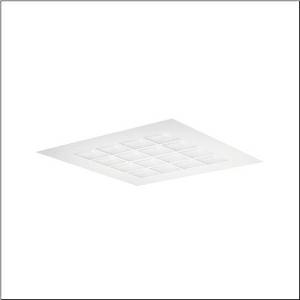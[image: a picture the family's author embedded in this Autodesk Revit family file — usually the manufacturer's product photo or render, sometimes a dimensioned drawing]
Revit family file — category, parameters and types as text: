
# Revit family: scriptus_11_5mz312ledzm00191xx
name_source: partatom
category: Lighting Fixtures
units: mm (PartAtom-declared; Revit-internal decimal feet)

## family parameters
Cut with Voids When Loaded = No
Host = Face
Light Source = No
Part Type = Normal
Room Calculation Point = No
Round Connector Dimension = Use Diameter
Shared = No

## types (1)
- Scriptus 11 (1 x LED, 6400 lm, 37.5 W, 4000K)
    Apparent Load = 38 VA
    CIE Flux Codes = 80 95 99 100 100
    Color Rendering = 80
    Color Temperature = 4000K
    Default Elevation = 1800 mm
    Description = Scriptus 11, office luminaire, primary optical cover: lenses, CAT 2 (L<= 3000cd/m²), light emission: direct distribution, primary light characteristic: symmetric, installation type: lay-in mounting, LED, rated luminous flux: 6.400lm, light colour: 840, colour temperature: 4000K, control gear: DALI, with terminal, 3+2-pole, max. 2.5mm², mains connection: 230V, AC, 50Hz, housing, of sheet steel, galvanised, traffic white (RAL 9016), module: M625, length: 621mm, width: 621mm, height: 68mm, protection rating (complete): IP20, insulation class (complete): insulation class I (protective earthing), certification: CE, impact resistance: IK02, permissible operating ambient temperature: 0..+35°C, standard: EN 50419, packaging unit: 1 piece
    Height = 80 mm  [stored 0.262467 ft]
    Lamp = 1 x LED
    Lamp Light Flux = 6400 lm
    Lamp Power = 37.5 W
    Lamp count = 1
    Length = 622 mm
    Luminous efficacy = 171 lm/W
    Manufacturer = Siteco
    ModVariant = No
    Model = 5MZ312LEDZM00191XX
    Mounting Place = Ceiling
    Mounting Type = Pendant
    Number of Poles = 1
    OnlyDefault = Yes
    Power Factor = 1
    Product Name = Scriptus 11
    Product group = office luminaire | ceiling pendant
    ProductGroupID = 903
    Protection Class = Protection class I
    Protection Degree = IP 20
    RLX_Detail_Level = 1
    RLX_Emergency_Light_Flux = 0 lm
    RLX_Emergency_Type = 0
    RLX_Emergency_Type_DB = No
    RlxData = <blob elided: 19009 chars, md5=5dd1bfea>
    Socket = socket
    Standby Power = 0 W
    System Light Flux = 6400 lm
    System Power = 38 W
    Type Comments = Product without accessories
    Type Image = l_1006857.jpg
    URL = http://relux.com
    VarID = ---
    Voltage = 0 V
    Weight = 0.00 kg
    Width = 622 mm

note: [stored X ft] marks values corroborated as IEEE doubles in the binary element streams (Revit-internal decimal feet)

## geometry (parser evidence)
native form markers: Blend x4, Sweep x10
no freeform markers — native parametric forms only
